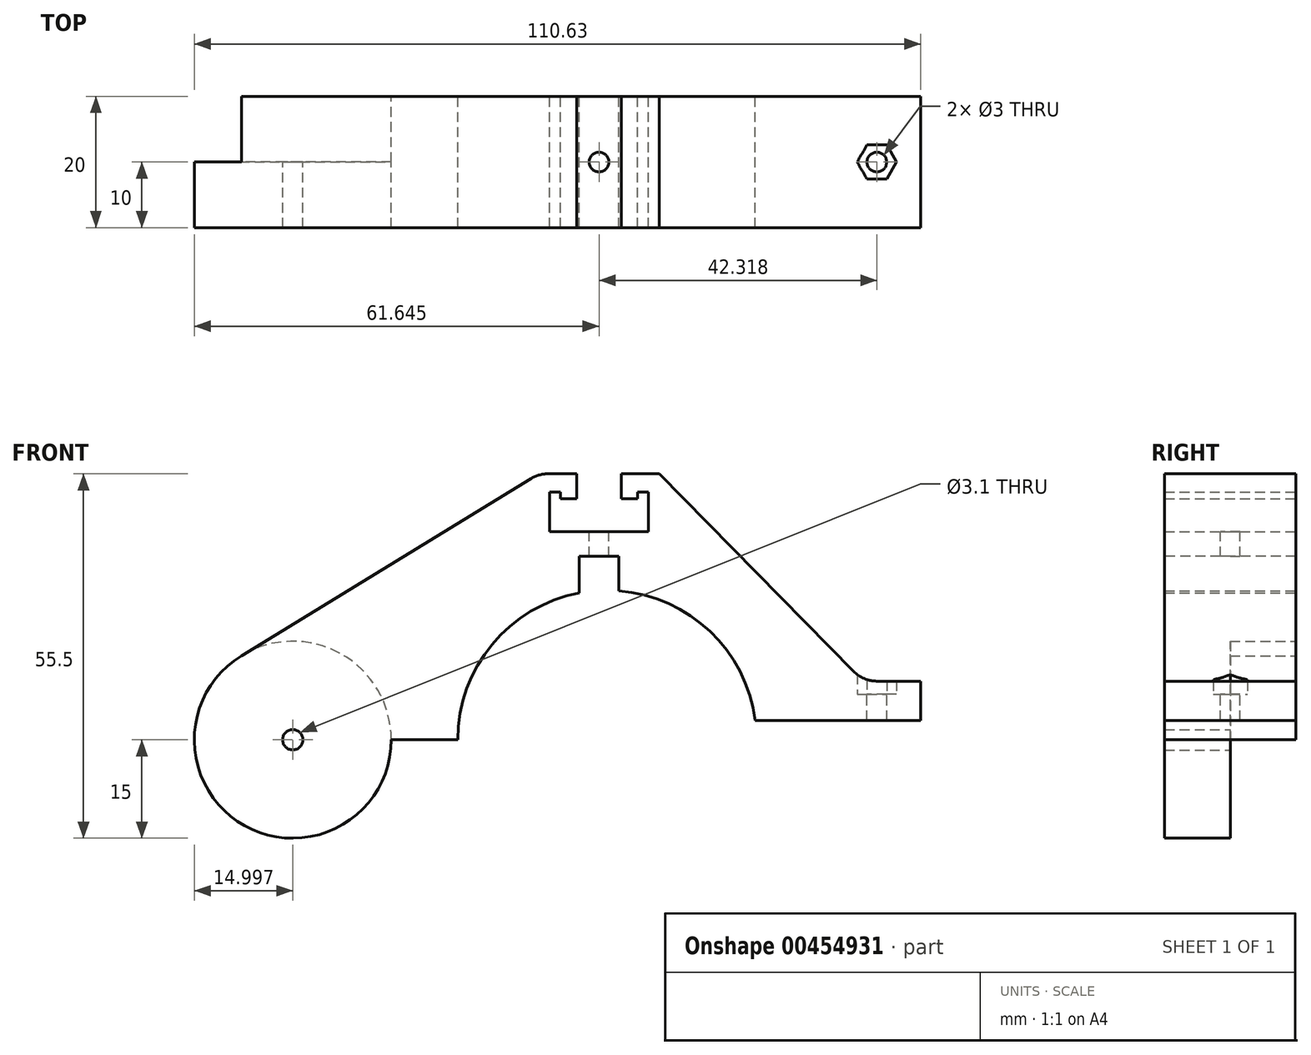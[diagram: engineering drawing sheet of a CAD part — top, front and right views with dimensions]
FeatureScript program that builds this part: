
annotation { "Feature Type Name" : "Feature", "Feature Type Description" : "" }
export const myFeature = defineFeature(function(context is Context, id is Id, definition is map)
    precondition{}
    {
        {
            var Q0;
            Q0=qCreatedBy(makeId("Front.planeOp"),FACE);
            var sketch = newSketch(context, id + "F0", { "sketchPlane" : qUnion([Q0])});
            skArc(sketch, "E0", {"start": v(22.56, 2.93) * mm, "mid": v(-1.47, 22.7) * mm, "end": v(-22.75, 0) * mm});
            skLineSegment(sketch, "E1", {"start": v(25.58, 2.93) * mm, "end": v(47.75, 2.93) * mm});
            skLineSegment(sketch, "E2", {"start": v(47.75, 2.93) * mm, "end": v(47.75, 8.93) * mm});
            skPoint(sketch, "E3.middle", {"position": v(0, 39.82) * mm});
            skLineSegment(sketch, "E4", {"start": v(25.58, 2.93) * mm, "end": v(22.56, 2.93) * mm});
            skCircle(sketch, "E5", {"center": v(-47.88, 0) * mm, "radius": 15 * mm});
            skLineSegment(sketch, "E6", {"start": v(-9.03, 40.5) * mm, "end": v(-4.64, 40.5) * mm});
            skLineSegment(sketch, "E7", {"start": v(-8.74, 37.7) * mm, "end": v(-8.74, 31.7) * mm});
            skLineSegment(sketch, "E8", {"start": v(-8.74, 31.7) * mm, "end": v(-1.24, 31.7) * mm});
            skLineSegment(sketch, "E9", {"start": v(-8.74, 37.7) * mm, "end": v(-7.14, 37.7) * mm});
            skLineSegment(sketch, "E10", {"start": v(-7.14, 37.7) * mm, "end": v(-7.14, 36.7) * mm});
            skLineSegment(sketch, "E11", {"start": v(-7.14, 36.7) * mm, "end": v(-4.64, 36.7) * mm});
            skLineSegment(sketch, "E12", {"start": v(-4.64, 36.7) * mm, "end": v(-4.64, 40.5) * mm});
            skLineSegment(sketch, "E13.MirrorCS", {"start": v(4.66, 37.7) * mm, "end": v(4.66, 36.7) * mm});
            skLineSegment(sketch, "E14.MirrorCS", {"start": v(4.66, 36.7) * mm, "end": v(2.16, 36.7) * mm});
            skLineSegment(sketch, "E15.MirrorCS", {"start": v(6.26, 37.7) * mm, "end": v(4.66, 37.7) * mm});
            skLineSegment(sketch, "E16.MirrorCS", {"start": v(2.16, 36.7) * mm, "end": v(2.16, 40.5) * mm});
            skLineSegment(sketch, "E17.MirrorCS", {"start": v(6.26, 37.7) * mm, "end": v(6.26, 31.7) * mm});
            skLineSegment(sketch, "E18.MirrorCS", {"start": v(7.96, 40.5) * mm, "end": v(2.16, 40.5) * mm});
            skLineSegment(sketch, "E19.MirrorCS", {"start": v(6.26, 31.7) * mm, "end": v(-1.24, 31.7) * mm});
            skLineSegment(sketch, "E20", {"start": v(-32.88, 0) * mm, "end": v(-25.75, 0) * mm});
            skCircle(sketch, "E21", {"center": v(-47.88, 0) * mm, "radius": 1.55 * mm});
            skLineSegment(sketch, "E22", {"start": v(-25.75, 0) * mm, "end": v(-22.75, 0) * mm});
            skLineSegment(sketch, "E23", {"start": v(-11.64, 39.77) * mm, "end": v(-55.71, 12.8) * mm});
            skPoint(sketch, "E24.visualSharp", {"position": v(-10.44, 40.5) * mm});
            skArc(sketch, "E24.filletArc", {"start": v(-9.03, 40.5) * mm, "mid": v(-10.38, 40.32) * mm, "end": v(-11.64, 39.77) * mm});
            skLineSegment(sketch, "E25", {"start": v(7.96, 40.5) * mm, "end": v(37.52, 10.42) * mm});
            skLineSegment(sketch, "E26", {"start": v(41.08, 8.93) * mm, "end": v(47.75, 8.93) * mm});
            skPoint(sketch, "E27.visualSharp", {"position": v(36.62, 11.34) * mm});
            skPoint(sketch, "E28.visualSharp", {"position": v(38.99, 8.93) * mm});
            skArc(sketch, "E28.filletArc", {"start": v(37.52, 10.42) * mm, "mid": v(39.15, 9.32) * mm, "end": v(41.08, 8.93) * mm});
            skSolve(sketch);
        }
        {
            var Q0;
            Q0=makeQuery(id+"F0.imprint","IMPRINT",FACE,{"disambiguationData":[TD([[makeQuery(id+"F0.imprint","IMPRINT",EDGE,{"derivedFrom":sQuery(id+"F0.wireOp",EDGE,"E0")}),-1.0]])]});
            extrude(context, id + "F1", {"entities" : qUnion([Q0]), "endBound" : BoundingType.SYMMETRIC, "depth" : 20 * mm});
        }
        {
            var Q0;
            Q0=makeQuery(id+"F0.imprint","IMPRINT",FACE,{"disambiguationData":[TD([[makeQuery(id+"F0.imprint","IMPRINT",EDGE,{"derivedFrom":sQuery(id+"F0.wireOp",EDGE,"E21")}),-1.0]])]});
            extrude(context, id + "F2", {"entities" : qUnion([Q0]), "operationType" : NewBodyOperationType.ADD, "depth" : 10 * mm});
        }
        {
            var Q0;
            Q0=makeQuery(id+"F1.opExtrude","SWEPT_FACE",FACE,{"disambiguationData":[OSD([sQuery(id+"F0.wireOp",EDGE,"E1"),sQuery(id+"F0.wireOp",EDGE,"E4")])]});
            var sketch = newSketch(context, id + "F3", { "sketchPlane" : qUnion([Q0])});
            skPoint(sketch, "E29.endSnap0", {"position": v(47.75, 0) * mm});
            skLineSegment(sketch, "E30.0", {"start": v(44.08, 0) * mm, "end": v(42.58, -2.6) * mm});
            skLineSegment(sketch, "E30.1", {"start": v(42.58, -2.6) * mm, "end": v(39.58, -2.6) * mm});
            skLineSegment(sketch, "E30.2", {"start": v(39.58, -2.6) * mm, "end": v(38.08, 0) * mm});
            skLineSegment(sketch, "E30.3", {"start": v(38.08, 0) * mm, "end": v(39.58, 2.6) * mm});
            skLineSegment(sketch, "E30.4", {"start": v(39.58, 2.6) * mm, "end": v(42.58, 2.6) * mm});
            skLineSegment(sketch, "E30.5", {"start": v(42.58, 2.6) * mm, "end": v(44.08, 0) * mm});
            skSolve(sketch);
        }
        {
            var Q0;
            Q0 = qSketchRegion(id + "F3", true);
            extrude(context, id + "F4", {"entities" : qUnion([Q0]), "operationType" : NewBodyOperationType.REMOVE, "oppositeDirection" : true, "depth" : 50 * mm});
        }
        {
            var Q0;
            Q0=makeQuery(id+"F1.opExtrude","SWEPT_FACE",FACE,{"disambiguationData":[OSD([sQuery(id+"F0.wireOp",EDGE,"E1"),sQuery(id+"F0.wireOp",EDGE,"E4")])]});
            var sketch = newSketch(context, id + "F5", { "sketchPlane" : qUnion([Q0])});
            skCircle(sketch, "E31.cCircle", {"center": v(41.08, 0) * mm, "radius": 3 * mm, "construction": true});
            skPoint(sketch, "E31.cCircle.centerSnap0", {"position": v(41.08, 2.6) * mm});
            skLineSegment(sketch, "E31.0", {"start": v(39.58, 2.6) * mm, "end": v(42.58, 2.6) * mm});
            skLineSegment(sketch, "E31.1", {"start": v(42.58, 2.6) * mm, "end": v(44.08, 0) * mm});
            skLineSegment(sketch, "E31.2", {"start": v(44.08, 0) * mm, "end": v(42.58, -2.6) * mm});
            skLineSegment(sketch, "E31.3", {"start": v(42.58, -2.6) * mm, "end": v(39.58, -2.6) * mm});
            skLineSegment(sketch, "E31.4", {"start": v(39.58, -2.6) * mm, "end": v(38.08, 0) * mm});
            skLineSegment(sketch, "E31.5", {"start": v(38.08, 0) * mm, "end": v(39.58, 2.6) * mm});
            skSolve(sketch);
        }
        {
            var Q0;
            Q0 = qSketchRegion(id + "F5", true);
            extrude(context, id + "F6", {"entities" : qUnion([Q0]), "operationType" : NewBodyOperationType.ADD, "depth" : -4 * mm});
        }
        {
            var Q0;
            Q0=makeQuery(id+"F6.opExtrude","CAP_FACE",FACE,{"disambiguationData":[OSD([sQuery(id+"F5.wireOp",EDGE,"E31.0"),sQuery(id+"F5.wireOp",EDGE,"E31.1"),sQuery(id+"F5.wireOp",EDGE,"E31.2"),sQuery(id+"F5.wireOp",EDGE,"E31.3"),sQuery(id+"F5.wireOp",EDGE,"E31.4"),sQuery(id+"F5.wireOp",EDGE,"E31.5")])],"isStart":false});
            var sketch = newSketch(context, id + "F7", { "sketchPlane" : qUnion([Q0])});
            skCircle(sketch, "E32", {"center": v(41.08, 0) * mm, "radius": 1.5 * mm});
            skPoint(sketch, "E32.centerSnap0", {"position": v(41.08, 2.6) * mm});
            skSolve(sketch);
        }
        {
            var Q0;
            Q0 = qSketchRegion(id + "F7", true);
            extrude(context, id + "F8", {"entities" : qUnion([Q0]), "operationType" : NewBodyOperationType.REMOVE, "oppositeDirection" : true, "depth" : 5 * mm});
        }
        {
            var Q0;
            Q0=makeQuery(id+"F6.boolean.opBoolean","MERGE",FACE,{"derivedFrom":[makeQuery(id+"F1.opExtrude","SWEPT_FACE",FACE,{"disambiguationData":[OSD([sQuery(id+"F0.wireOp",EDGE,"E1"),sQuery(id+"F0.wireOp",EDGE,"E4")])]}),makeQuery(id+"F6.opExtrude","CAP_FACE",FACE,{"disambiguationData":[OSD([sQuery(id+"F5.wireOp",EDGE,"E31.0"),sQuery(id+"F5.wireOp",EDGE,"E31.1"),sQuery(id+"F5.wireOp",EDGE,"E31.2"),sQuery(id+"F5.wireOp",EDGE,"E31.3"),sQuery(id+"F5.wireOp",EDGE,"E31.4"),sQuery(id+"F5.wireOp",EDGE,"E31.5")])],"isStart":true})]});
            var sketch = newSketch(context, id + "F9", { "sketchPlane" : qUnion([Q0])});
            skPoint(sketch, "E33.0", {"position": v(-1.24, 0) * mm});
            skCircle(sketch, "E34", {"center": v(-1.24, 0) * mm, "radius": 1.5 * mm});
            skPoint(sketch, "E35.0", {"position": v(22.56, 10) * mm});
            skPoint(sketch, "E36.0", {"position": v(-22.75, 10) * mm});
            skPoint(sketch, "E37.0", {"position": v(-22.75, -10) * mm});
            skPoint(sketch, "E38.0", {"position": v(22.56, -10) * mm});
            skLineSegment(sketch, "E39", {"start": v(-22.75, -10) * mm, "end": v(22.56, -10) * mm});
            skLineSegment(sketch, "E40", {"start": v(-1.24, -10) * mm, "end": v(-4.24, -10) * mm});
            skLineSegment(sketch, "E41", {"start": v(-4.24, -10) * mm, "end": v(3.76, -10) * mm});
            skLineSegment(sketch, "E42", {"start": v(-1.24, -10) * mm, "end": v(1.76, -10) * mm});
            skLineSegment(sketch, "E43", {"start": v(1.76, 10) * mm, "end": v(-4.24, 10) * mm});
            skLineSegment(sketch, "E44", {"start": v(-4.24, 10) * mm, "end": v(-4.24, -10) * mm});
            skLineSegment(sketch, "E45", {"start": v(1.76, -10) * mm, "end": v(1.76, 10) * mm});
            skLineSegment(sketch, "E46.0", {"start": v(22.56, 10) * mm, "end": v(-22.75, 10) * mm});
            skSolve(sketch);
        }
        {
            var Q0;
            Q0=makeQuery(id+"F9.imprint","IMPRINT",FACE,{"disambiguationData":[TD([[makeQuery(id+"F9.imprint","IMPRINT",EDGE,{"derivedFrom":sQuery(id+"F9.wireOp",EDGE,"E34")}),-1.0]])]});
            extrude(context, id + "F10", {"entities" : qUnion([Q0]), "operationType" : NewBodyOperationType.REMOVE, "oppositeDirection" : true, "depth" : 25 * mm});
        }
        {
            var Q0;
            Q0=makeQuery(id+"F1.opExtrude","SWEPT_FACE",FACE,{"disambiguationData":[OSD([sQuery(id+"F0.wireOp",EDGE,"E8"),sQuery(id+"F0.wireOp",EDGE,"E19.MirrorCS")])]});
            var sketch = newSketch(context, id + "F11", { "sketchPlane" : qUnion([Q0])});
            skCircle(sketch, "E47.0", {"center": v(-1.24, 0) * mm, "radius": 1.5 * mm});
            skSolve(sketch);
        }
        {
            var Q0;
            Q0 = qSketchRegion(id + "F11", true);
            extrude(context, id + "F12", {"entities" : qUnion([Q0]), "operationType" : NewBodyOperationType.REMOVE, "oppositeDirection" : true, "depth" : 25 * mm});
        }
    });
